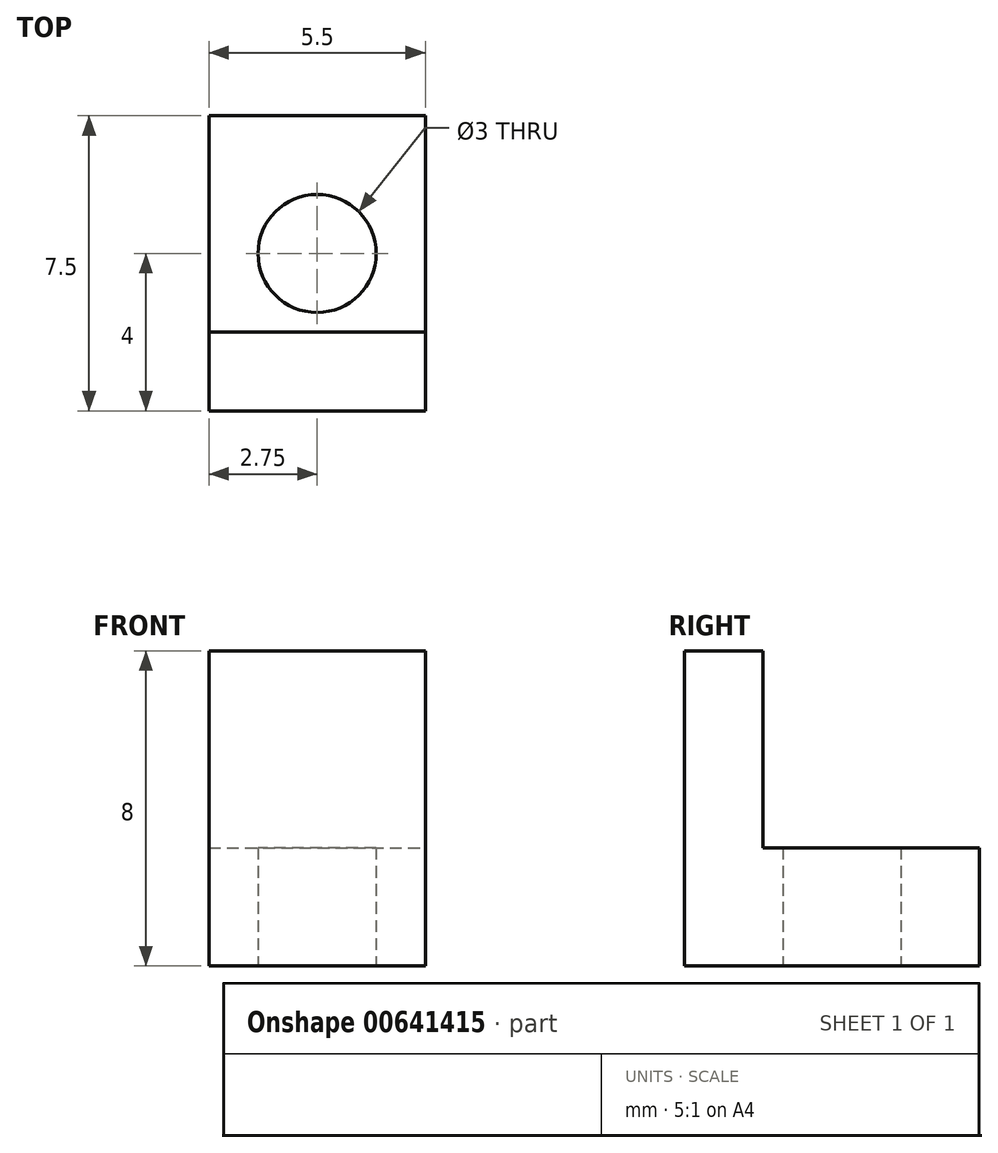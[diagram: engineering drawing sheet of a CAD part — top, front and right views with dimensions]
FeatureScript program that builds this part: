
annotation { "Feature Type Name" : "Feature", "Feature Type Description" : "" }
export const myFeature = defineFeature(function(context is Context, id is Id, definition is map)
    precondition{}
    {
        {
            var Q0;
            Q0=qCreatedBy(makeId("Top.planeOp"),FACE);
            var sketch = newSketch(context, id + "F0", { "sketchPlane" : qUnion([Q0])});
            skLineSegment(sketch, "E0.bottom", {"start": v(-2.75, 2.75) * mm, "end": v(2.75, 2.75) * mm});
            skLineSegment(sketch, "E0.top", {"start": v(-2.75, -2.75) * mm, "end": v(2.75, -2.75) * mm});
            skLineSegment(sketch, "E0.left", {"start": v(-2.75, 2.75) * mm, "end": v(-2.75, -2.75) * mm});
            skLineSegment(sketch, "E0.right", {"start": v(2.75, 2.75) * mm, "end": v(2.75, -2.75) * mm});
            skPoint(sketch, "E0.middle", {"position": v(0, 0) * mm});
            skLineSegment(sketch, "E1.top", {"start": v(-2.75, -4.75) * mm, "end": v(2.75, -4.75) * mm});
            skLineSegment(sketch, "E1.left", {"start": v(-2.75, -2.75) * mm, "end": v(-2.75, -4.75) * mm});
            skLineSegment(sketch, "E1.right", {"start": v(2.75, -2.75) * mm, "end": v(2.75, -4.75) * mm});
            skCircle(sketch, "E2", {"center": v(0, -0.75) * mm, "radius": 1.5 * mm});
            skSolve(sketch);
        }
        {
            var Q0;
            Q0=makeQuery(id+"F0.imprint","IMPRINT",FACE,{"disambiguationData":[TD([[makeQuery(id+"F0.imprint","IMPRINT",EDGE,{"derivedFrom":sQuery(id+"F0.wireOp",EDGE,"E0.bottom")}),-1.0]])]});
            var Q1;
            Q1=makeQuery(id+"F0.imprint","IMPRINT",FACE,{"disambiguationData":[TD([[makeQuery(id+"F0.imprint","IMPRINT",EDGE,{"derivedFrom":sQuery(id+"F0.wireOp",EDGE,"E0.top")}),-1.0]])]});
            extrude(context, id + "F1", {"entities" : qUnion([Q0, Q1]), "depth" : 3 * mm, "offsetDistance" : 25 * mm});
        }
        {
            var Q0;
            Q0=makeQuery(id+"F0.imprint","IMPRINT",FACE,{"disambiguationData":[TD([[makeQuery(id+"F0.imprint","IMPRINT",EDGE,{"derivedFrom":sQuery(id+"F0.wireOp",EDGE,"E0.top")}),-1.0]])]});
            extrude(context, id + "F2", {"entities" : qUnion([Q0]), "operationType" : NewBodyOperationType.ADD, "depth" : 8 * mm, "offsetDistance" : 25 * mm});
        }
    });
